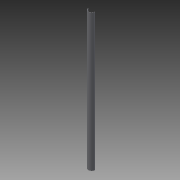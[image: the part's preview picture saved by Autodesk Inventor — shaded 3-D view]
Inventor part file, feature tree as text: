
AUTODESK INVENTOR PART (.ipt)
format: ipt  version: 2015 SP1 (Build 190203100, 203)  size: 83,456 bytes
history: native  units: mm
features: other x3, sketch x2
ambient origin geometry x8: Origin, YZ Plane, XZ Plane, XY Plane, X Axis, Y Axis, Z Axis, Center Point
bodies: Solid1 (feature_tree)
feature tree (5):
  other  "Tube sous miroir.ipt"
  other  "Solid1::Tube sous miroir.ipt"
  other  "TaggingFeature1"
  sketch  "Sketch1"  dims[d0=10.0mm]
  sketch  "Sketch2"
